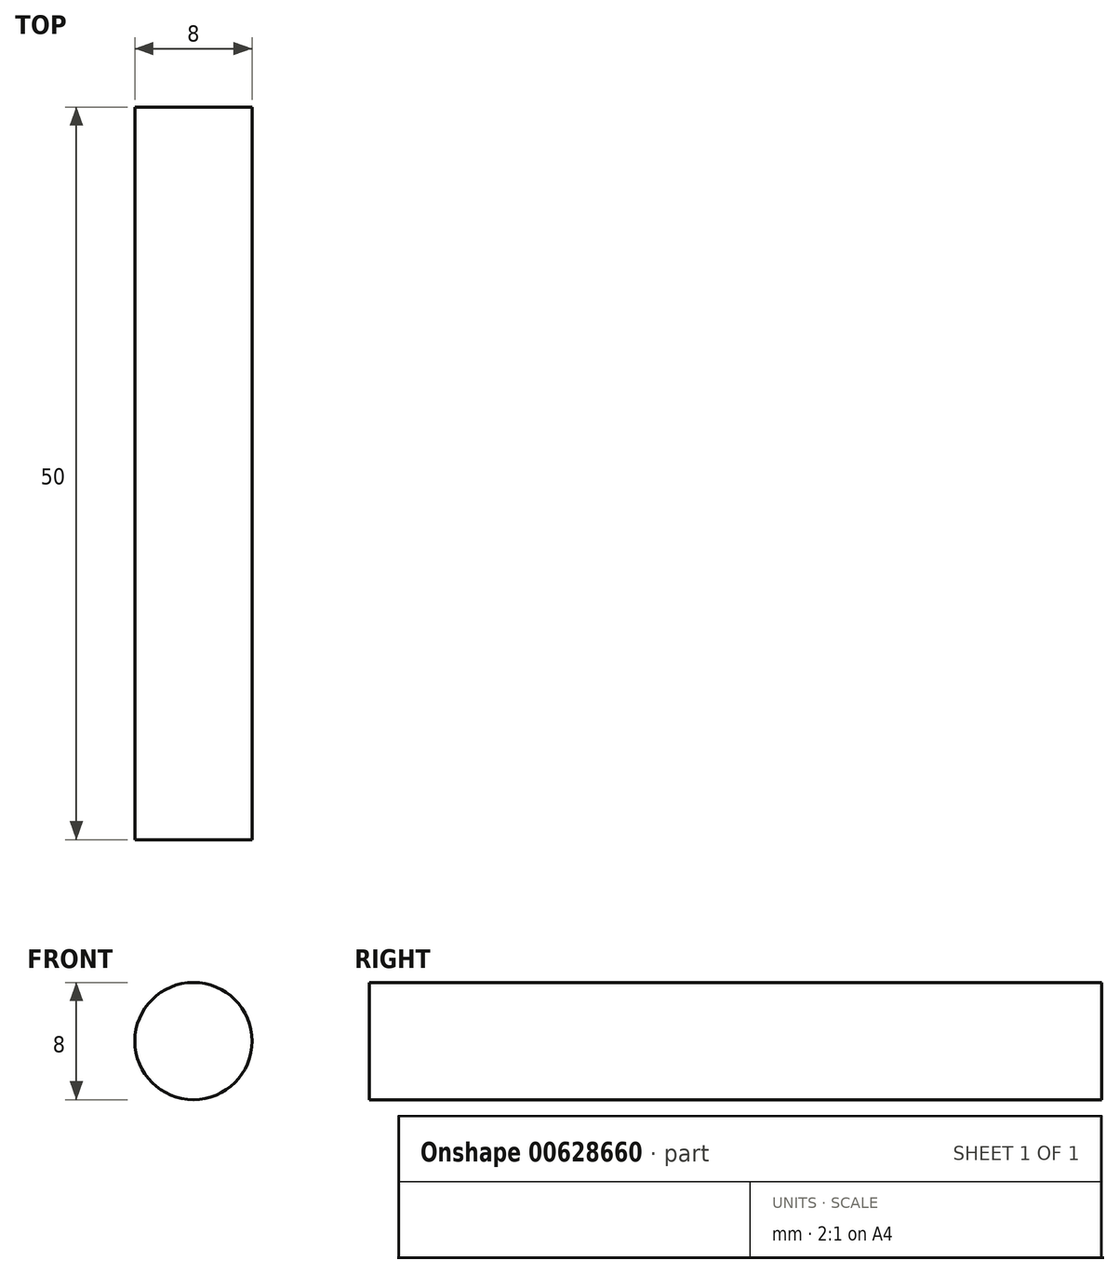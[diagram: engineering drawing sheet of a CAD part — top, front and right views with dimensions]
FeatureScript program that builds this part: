
annotation { "Feature Type Name" : "Feature", "Feature Type Description" : "" }
export const myFeature = defineFeature(function(context is Context, id is Id, definition is map)
    precondition{}
    {
        {
            var Q0;
            Q0=qCreatedBy(makeId("Front.planeOp"),FACE);
            var sketch = newSketch(context, id + "F0", { "sketchPlane" : qUnion([Q0])});
            skCircle(sketch, "E0", {"center": v(0, 0) * mm, "radius": 4 * mm});
            skSolve(sketch);
        }
        {
            var Q0;
            Q0=makeQuery(id+"F0.imprint","IMPRINT",FACE,{"disambiguationData":[TD([[makeQuery(id+"F0.imprint","IMPRINT",EDGE,{"derivedFrom":sQuery(id+"F0.wireOp",EDGE,"E0")}),1.0]])]});
            extrude(context, id + "F1", {"entities" : qUnion([Q0]), "endBound" : BoundingType.SYMMETRIC, "depth" : 50 * mm, "offsetDistance" : 25 * mm});
        }
    });
